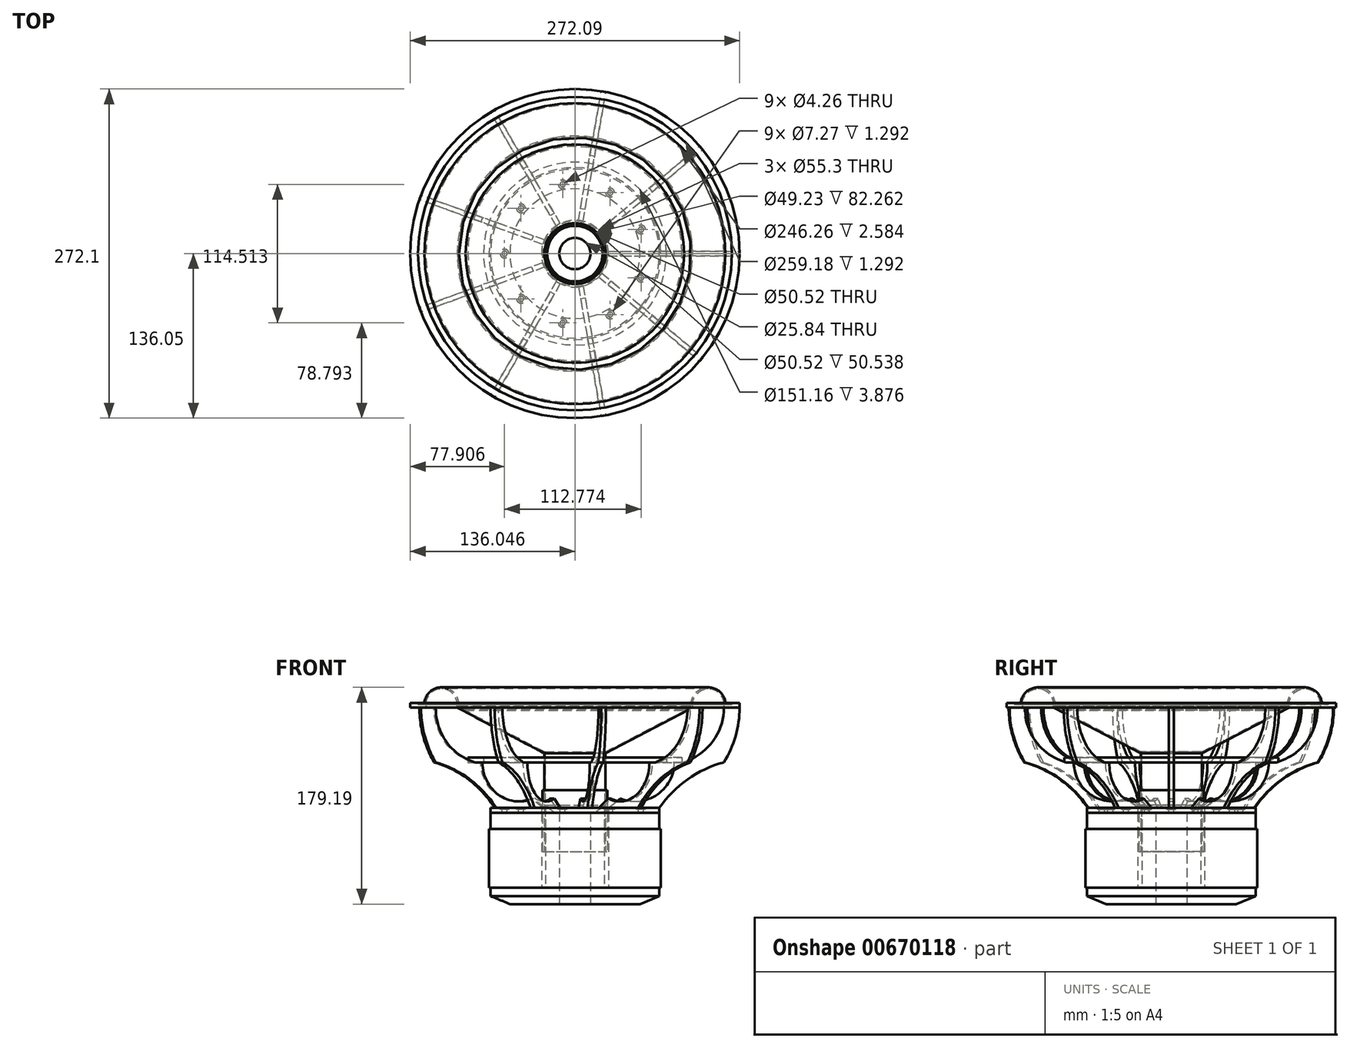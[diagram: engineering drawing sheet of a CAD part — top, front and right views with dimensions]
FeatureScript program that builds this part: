
annotation { "Feature Type Name" : "Feature", "Feature Type Description" : "" }
export const myFeature = defineFeature(function(context is Context, id is Id, definition is map)
    precondition{}
    {
        {
            var Q0;
            Q0=qCreatedBy(makeId("Front.planeOp"),FACE);
            var sketch = newSketch(context, id + "F0", { "sketchPlane" : qUnion([Q0])});
            skLineSegment(sketch, "E0.bottom", {"start": v(42.8, 0) * mm, "end": v(108, 0) * mm});
            skLineSegment(sketch, "E0.top", {"start": v(42.8, -6) * mm, "end": v(108, -6) * mm});
            skLineSegment(sketch, "E0.left", {"start": v(42.8, 0) * mm, "end": v(42.8, -6) * mm});
            skLineSegment(sketch, "E1", {"start": v(108, -6) * mm, "end": v(108, 0) * mm});
            skLineSegment(sketch, "E2", {"start": v(0, 0) * mm, "end": v(0, 32.36) * mm, "construction": true});
            skLineSegment(sketch, "E3.bottom", {"start": v(200.6, 134.34) * mm, "end": v(210.6, 134.34) * mm});
            skLineSegment(sketch, "E3.top", {"start": v(190.6, 128.34) * mm, "end": v(210.6, 128.34) * mm});
            skLineSegment(sketch, "E3.left", {"start": v(190.6, 132.34) * mm, "end": v(190.6, 128.34) * mm});
            skLineSegment(sketch, "E3.right", {"start": v(210.6, 134.34) * mm, "end": v(210.6, 128.34) * mm});
            skLineSegment(sketch, "E4", {"start": v(150.6, 128.34) * mm, "end": v(39.1, 70.03) * mm});
            skLineSegment(sketch, "E5", {"start": v(150.6, 130.03) * mm, "end": v(150.6, 128.34) * mm});
            skLineSegment(sketch, "E6", {"start": v(39.1, 71.72) * mm, "end": v(39.1, 70.03) * mm});
            skLineSegment(sketch, "E7.top", {"start": v(38.1, 71.72) * mm, "end": v(39.1, 71.72) * mm});
            skLineSegment(sketch, "E7.right", {"start": v(39.1, -55.62) * mm, "end": v(39.1, 71.72) * mm});
            skLineSegment(sketch, "E8", {"start": v(38.1, 71.72) * mm, "end": v(38.1, -55.62) * mm});
            skLineSegment(sketch, "E9", {"start": v(150.6, 130.03) * mm, "end": v(0, 130.03) * mm, "construction": true});
            skArc(sketch, "E10", {"start": v(0, 112.72) * mm, "mid": v(42.04, 108.02) * mm, "end": v(82, 94.16) * mm});
            skLineSegment(sketch, "E11", {"start": v(0, 112.72) * mm, "end": v(0, 111.72) * mm});
            skArc(sketch, "E12", {"start": v(0, 111.72) * mm, "mid": v(41.06, 106.82) * mm, "end": v(80.09, 93.16) * mm});
            skLineSegment(sketch, "E13", {"start": v(150.6, 130.03) * mm, "end": v(39.1, 71.72) * mm});
            skLineSegment(sketch, "E14", {"start": v(0, 112.72) * mm, "end": v(-8.95, 112.72) * mm, "construction": true});
            skLineSegment(sketch, "E15", {"start": v(190.6, 132.34) * mm, "end": v(200.6, 132.34) * mm});
            skLineSegment(sketch, "E16", {"start": v(200.6, 132.34) * mm, "end": v(200.6, 134.34) * mm});
            skLineSegment(sketch, "E17.right", {"start": v(110, -27) * mm, "end": v(110, -102) * mm});
            skLineSegment(sketch, "E18.top", {"start": v(108, -6) * mm, "end": v(42.8, -6) * mm});
            skLineSegment(sketch, "E18.left", {"start": v(108, -27) * mm, "end": v(108, -6) * mm});
            skLineSegment(sketch, "E18.right", {"start": v(42.8, -27) * mm, "end": v(42.8, -6) * mm});
            skLineSegment(sketch, "E19.top", {"start": v(83.05, -123) * mm, "end": v(20, -123) * mm});
            skLineSegment(sketch, "E19.left", {"start": v(108, -102) * mm, "end": v(108, -112.7) * mm});
            skLineSegment(sketch, "E19.right", {"start": v(20, -102) * mm, "end": v(20, -123) * mm});
            skLineSegment(sketch, "E20", {"start": v(108, -112.7) * mm, "end": v(83.05, -123) * mm});
            skPoint(sketch, "E21", {"position": v(42.8, -16.5) * mm});
            skLineSegment(sketch, "E22", {"start": v(139.64, 126.56) * mm, "end": v(140.57, 124.79) * mm});
            skArc(sketch, "E23", {"start": v(190.6, 132.34) * mm, "mid": v(169.38, 152.37) * mm, "end": v(150.6, 130.03) * mm});
            skLineSegment(sketch, "E24", {"start": v(200.6, 134.34) * mm, "end": v(192.5, 134.34) * mm});
            skLineSegment(sketch, "E25", {"start": v(139.64, 126.56) * mm, "end": v(148.5, 131.2) * mm});
            skArc(sketch, "E26", {"start": v(192.5, 134.34) * mm, "mid": v(168.96, 154.34) * mm, "end": v(148.5, 131.2) * mm});
            skLineSegment(sketch, "E27", {"start": v(192.5, 134.34) * mm, "end": v(190.5, 134.34) * mm, "construction": true});
            skLineSegment(sketch, "E28", {"start": v(127, 58.38) * mm, "end": v(127, 64.38) * mm});
            skLineSegment(sketch, "E29", {"start": v(117, 58.38) * mm, "end": v(42.8, 0) * mm, "construction": true});
            skLineSegment(sketch, "E30", {"start": v(150.6, 128.34) * mm, "end": v(150.6, 69.15) * mm, "construction": true});
            skCircle(sketch, "E31", {"center": v(170.53, 132.34) * mm, "radius": 20.07 * mm, "construction": true});
            skLineSegment(sketch, "E32", {"start": v(190.6, 128.34) * mm, "end": v(150.6, 69.15) * mm, "construction": true});
            skArc(sketch, "E33", {"start": v(190.46, 58.38) * mm, "mid": v(205.46, 91.94) * mm, "end": v(210.6, 128.34) * mm});
            skLineSegment(sketch, "E34.left", {"start": v(117, 58.38) * mm, "end": v(117, 64.38) * mm});
            skPoint(sketch, "E34.middle", {"position": v(127, 61.38) * mm});
            skLineSegment(sketch, "E35", {"start": v(137, 58.38) * mm, "end": v(137, 64.38) * mm});
            skLineSegment(sketch, "E36", {"start": v(137, 64.38) * mm, "end": v(117, 64.38) * mm});
            skArc(sketch, "E37", {"start": v(190.6, 128.34) * mm, "mid": v(175.66, 84.27) * mm, "end": v(137, 58.38) * mm});
            skPoint(sketch, "E38.endSnap0", {"position": v(75.4, 0) * mm});
            skLineSegment(sketch, "E39", {"start": v(42.8, 0) * mm, "end": v(58.05, 12) * mm});
            skLineSegment(sketch, "E40", {"start": v(58.05, 12) * mm, "end": v(58.05, 0) * mm});
            skArc(sketch, "E41", {"start": v(127, 58.38) * mm, "mid": v(104.88, 16.83) * mm, "end": v(58.05, 12) * mm});
            skLineSegment(sketch, "E42", {"start": v(127, 58.38) * mm, "end": v(137, 58.38) * mm});
            skLineSegment(sketch, "E43", {"start": v(127, 58.38) * mm, "end": v(117, 58.38) * mm});
            skLineSegment(sketch, "E44", {"start": v(117, 64.38) * mm, "end": v(117, 110.77) * mm, "construction": true});
            skLineSegment(sketch, "E45", {"start": v(196.55, 134.34) * mm, "end": v(196.55, 140.34) * mm});
            skLineSegment(sketch, "E46", {"start": v(196.55, 140.34) * mm, "end": v(226.55, 140.34) * mm});
            skLineSegment(sketch, "E47", {"start": v(226.55, 140.34) * mm, "end": v(226.55, 134.34) * mm});
            skLineSegment(sketch, "E48", {"start": v(226.55, 134.34) * mm, "end": v(210.6, 134.34) * mm});
            skLineSegment(sketch, "E49", {"start": v(38.1, -55.62) * mm, "end": v(41.66, -55.62) * mm});
            skLineSegment(sketch, "E50", {"start": v(41.66, -55.62) * mm, "end": v(41.66, 22.62) * mm});
            skLineSegment(sketch, "E51", {"start": v(41.66, 22.62) * mm, "end": v(39.1, 22.62) * mm});
            skLineSegment(sketch, "E52", {"start": v(42.8, -27) * mm, "end": v(42.8, -102) * mm});
            skPoint(sketch, "E53", {"position": v(41.66, -16.5) * mm});
            skLineSegment(sketch, "E54", {"start": v(42.8, -27) * mm, "end": v(110, -27) * mm});
            skLineSegment(sketch, "E55", {"start": v(20, -102) * mm, "end": v(110, -102) * mm});
            skLineSegment(sketch, "E56", {"start": v(110, -52.4) * mm, "end": v(42.8, -52.4) * mm});
            skLineSegment(sketch, "E57", {"start": v(110, -76.6) * mm, "end": v(42.8, -76.6) * mm});
            skArc(sketch, "E58", {"start": v(190.46, 58.38) * mm, "mid": v(143.97, 36.62) * mm, "end": v(108, 0) * mm});
            skLineSegment(sketch, "E59", {"start": v(39.1, -55.62) * mm, "end": v(39.1, -102) * mm, "construction": true});
            skLineSegment(sketch, "E60", {"start": v(58.05, 12) * mm, "end": v(58.05, 58.38) * mm, "construction": true});
            skLineSegment(sketch, "E61", {"start": v(20, -102) * mm, "end": v(20, -6) * mm});
            skLineSegment(sketch, "E62", {"start": v(37.5, -102) * mm, "end": v(37.5, 3.38) * mm});
            skArc(sketch, "E63", {"start": v(20, -6) * mm, "mid": v(29.06, -3.47) * mm, "end": v(35.5, 3.38) * mm});
            skLineSegment(sketch, "E64", {"start": v(20, -6) * mm, "end": v(0, -6) * mm, "construction": true});
            skLineSegment(sketch, "E65", {"start": v(35.5, 3.38) * mm, "end": v(37.5, 3.38) * mm});
            skSolve(sketch);
        }
        {
            var Q0;
            Q0=makeQuery(id+"F0.imprint","IMPRINT",FACE,{"disambiguationData":[TD([[makeQuery(id+"F0.imprint","IMPRINT",EDGE,{"derivedFrom":sQuery(id+"F0.wireOp",EDGE,"E0.bottom")}),1.0]])]});
            var Q1;
            Q1=makeQuery(id+"F0.imprint","IMPRINT",FACE,{"disambiguationData":[TD([[makeQuery(id+"F0.imprint","IMPRINT",EDGE,{"derivedFrom":sQuery(id+"F0.wireOp",EDGE,"E3.top")}),-1.0]])]});
            extrude(context, id + "F1", {"entities" : qUnion([Q0, Q1]), "depth" : 3 * mm, "hasSecondDirection" : true, "secondDirectionOppositeDirection" : true, "secondDirectionDepth" : 3 * mm});
        }
        {
            var Q0;
            Q0=makeQuery(id+"F1.opExtrude","SWEPT_BODY",BODY,{"disambiguationData":[OSD([sQuery(id+"F0.wireOp",EDGE,"E0.bottom"),sQuery(id+"F0.wireOp",EDGE,"6c7cb310-9df3-4df2-87a5-b65033ba0822.top"),sQuery(id+"F0.wireOp",EDGE,"nT3Qd54m-n4Mr-KzPj-ubfg-OKSk5NO6LqhC"),sQuery(id+"F0.wireOp",EDGE,"HfDnNz2e-wXp7-ltQI-1r98-O9Q1wdCByFx3"),sQuery(id+"F0.wireOp",EDGE,"b51f060f-5979-43c8-a97c-01c7b52eec3f")])]});
            var Q1;
            Q1=makeQuery(id+"F1.opExtrude","SWEPT_BODY",BODY,{"disambiguationData":[OSD([sQuery(id+"F0.wireOp",EDGE,"56108468-e6ef-4c31-aa1b-a381e27727b4.top"),sQuery(id+"F0.wireOp",EDGE,"E3.top"),sQuery(id+"F0.wireOp",EDGE,"4c3c0eb7-8127-4a6f-916d-201b3557d1e0"),sQuery(id+"F0.wireOp",EDGE,"e00a4080-055f-4dc8-8bab-c810e85ee1ca"),sQuery(id+"F0.wireOp",EDGE,"936a3c3a-1da7-4d78-9b4e-07095c25ca2c"),sQuery(id+"F0.wireOp",EDGE,"0a553143-d006-4ff2-9b8a-ab2828d84b0a")])]});
            var Q2;
            Q2=sQuery(id+"F0.wireOp",EDGE,"E2");
            circularPattern(context, id + "F2", {"entities" : qUnion([Q0, Q1]), "axis" : qUnion([Q2]), "angle" : 360 * degree, "instanceCount" : 9, "equalSpace" : true});
        }
        {
            var Q0;
            Q0=makeQuery(id+"F0.imprint","IMPRINT",FACE,{"disambiguationData":[TD([[makeQuery(id+"F0.imprint","IMPRINT",EDGE,{"derivedFrom":sQuery(id+"F0.wireOp",EDGE,"E0.bottom")}),-1.0]])]});
            var Q1;
            Q1=makeQuery(id+"F0.imprint","IMPRINT",FACE,{"disambiguationData":[TD([[makeQuery(id+"F0.imprint","IMPRINT",EDGE,{"derivedFrom":sQuery(id+"F0.wireOp",EDGE,"E4")}),-1.0]])]});
            var Q2;
            Q2=makeQuery(id+"F0.imprint","IMPRINT",FACE,{"disambiguationData":[TD([[makeQuery(id+"F0.imprint","IMPRINT",EDGE,{"derivedFrom":sQuery(id+"F0.wireOp",EDGE,"E3.bottom")}),-1.0]])]});
            var Q3;
            {var subQ0=sQuery(id+"F0.wireOp",EDGE,"E28");Q3=makeQuery(id+"F0.imprint","IMPRINT",FACE,{"disambiguationData":[TD([[makeQuery(id+"F0.imprint","IMPRINT",EDGE,{"derivedFrom":subQ0}),-1.0]])]});}
            var Q4;
            {var subQ0=sQuery(id+"F0.wireOp",EDGE,"E28");Q4=makeQuery(id+"F0.imprint","IMPRINT",FACE,{"disambiguationData":[TD([[makeQuery(id+"F0.imprint","IMPRINT",EDGE,{"derivedFrom":subQ0}),1.0]])]});}
            var Q5;
            {var subQ6=sQuery(id+"F0.wireOp",EDGE,"E56");Q5=makeQuery(id+"F0.imprint","IMPRINT",FACE,{"disambiguationData":[TD([[makeQuery(id+"F0.imprint","IMPRINT",EDGE,{"derivedFrom":subQ6}),-1.0]])]});}
            var Q6;
            {var subQ0=sQuery(id+"F0.wireOp",EDGE,"E56");Q6=makeQuery(id+"F0.imprint","IMPRINT",FACE,{"disambiguationData":[TD([[makeQuery(id+"F0.imprint","IMPRINT",EDGE,{"derivedFrom":subQ0}),1.0]])]});}
            var Q7;
            {var subQ6=sQuery(id+"F0.wireOp",EDGE,"E57");Q7=makeQuery(id+"F0.imprint","IMPRINT",FACE,{"disambiguationData":[TD([[makeQuery(id+"F0.imprint","IMPRINT",EDGE,{"derivedFrom":subQ6}),1.0]])]});}
            var Q8;
            {var subQ4=sQuery(id+"F0.wireOp",EDGE,"E50");Q8=makeQuery(id+"F0.imprint","IMPRINT",FACE,{"disambiguationData":[TD([[makeQuery(id+"F0.imprint","IMPRINT",EDGE,{"derivedFrom":subQ4}),1.0]])]});}
            var Q9;
            Q9=sQuery(id+"F0.wireOp",EDGE,"E2");
            revolve(context, id + "F3", {"entities" : qUnion([Q0, Q1, Q2, Q3, Q4, Q5, Q6, Q7, Q8]), "axis" : qUnion([Q9]), "revolveType" : RevolveType.FULL});
        }
        {
            var Q0;
            {var subQ5=sQuery(id+"F0.wireOp",EDGE,"E7.top");Q0=makeQuery(id+"F0.imprint","IMPRINT",FACE,{"disambiguationData":[TD([[makeQuery(id+"F0.imprint","IMPRINT",EDGE,{"derivedFrom":subQ5}),-1.0]])]});}
            var Q1;
            {var subQ0=sQuery(id+"F0.wireOp",EDGE,"E10");Q1=makeQuery(id+"F0.imprint","IMPRINT",FACE,{"disambiguationData":[TD([[makeQuery(id+"F0.imprint","IMPRINT",EDGE,{"derivedFrom":subQ0}),-1.0]])]});}
            var Q2;
            {var subQ3=sQuery(id+"F0.wireOp",EDGE,"E18.left");Q2=makeQuery(id+"F0.imprint","IMPRINT",FACE,{"disambiguationData":[TD([[makeQuery(id+"F0.imprint","IMPRINT",EDGE,{"derivedFrom":subQ3}),1.0]])]});}
            var Q3;
            Q3=makeQuery(id+"F0.imprint","IMPRINT",FACE,{"disambiguationData":[TD([[makeQuery(id+"F0.imprint","IMPRINT",EDGE,{"derivedFrom":sQuery(id+"F0.wireOp",EDGE,"E19.top")}),-1.0]])]});
            var Q4;
            Q4=makeQuery(id+"F0.imprint","IMPRINT",FACE,{"disambiguationData":[TD([[makeQuery(id+"F0.imprint","IMPRINT",EDGE,{"derivedFrom":sQuery(id+"F0.wireOp",EDGE,"E15")}),1.0]])]});
            var Q5;
            {var subQ1=sQuery(id+"F0.wireOp",EDGE,"E61");Q5=makeQuery(id+"F0.imprint","IMPRINT",FACE,{"disambiguationData":[TD([[makeQuery(id+"F0.imprint","IMPRINT",EDGE,{"derivedFrom":subQ1}),-1.0]])]});}
            var Q6;
            Q6=sQuery(id+"F0.wireOp",EDGE,"E2");
            revolve(context, id + "F4", {"entities" : qUnion([Q0, Q1, Q2, Q3, Q4, Q5]), "axis" : qUnion([Q6]), "revolveType" : RevolveType.FULL});
        }
        {
            var Q0;
            Q0=makeQuery(id+"F3.opRevolve","SWEPT_FACE",FACE,{"disambiguationData":[OSD([sQuery(id+"F0.wireOp",EDGE,"E0.bottom")])]});
            var sketch = newSketch(context, id + "F5", { "sketchPlane" : qUnion([Q0])});
            skPoint(sketch, "E66", {"position": v(-90, 0) * mm});
            skPoint(sketch, "E67.1.0", {"position": v(-68.94, -57.85) * mm});
            skPoint(sketch, "E67.2.0", {"position": v(-15.63, -88.63) * mm});
            skPoint(sketch, "E67.3.0", {"position": v(45, -77.94) * mm});
            skPoint(sketch, "E67.4.0", {"position": v(84.57, -30.78) * mm});
            skPoint(sketch, "E67.center", {"position": v(0, 0) * mm});
            skPoint(sketch, "E68.0.5.0", {"position": v(84.57, 30.78) * mm});
            skPoint(sketch, "E69.0.6.0", {"position": v(45, 77.94) * mm});
            skPoint(sketch, "E69.0.7.0", {"position": v(-15.63, 88.63) * mm});
            skPoint(sketch, "E69.0.8.0", {"position": v(-68.94, 57.85) * mm});
            skSolve(sketch);
        }
        {
            var Q0;
            Q0=sQuery(id+"F5.wireOp",VERTEX,"E66");
            var Q1;
            Q1=sQuery(id+"F5.wireOp",VERTEX,"E67.4.0");
            var Q2;
            Q2=sQuery(id+"F5.wireOp",VERTEX,"E67.3.0");
            var Q3;
            Q3=sQuery(id+"F5.wireOp",VERTEX,"E67.2.0");
            var Q4;
            Q4=sQuery(id+"F5.wireOp",VERTEX,"E67.1.0");
            var Q5;
            Q5=sQuery(id+"F5.wireOp",VERTEX,"E68.0.5.0");
            var Q6;
            Q6=sQuery(id+"F5.wireOp",VERTEX,"E69.0.7.0");
            var Q7;
            Q7=sQuery(id+"F5.wireOp",VERTEX,"E69.0.8.0");
            var Q8;
            Q8=sQuery(id+"F5.wireOp",VERTEX,"E69.0.6.0");
            var Q9;
            Q9=makeQuery(id+"F3.opRevolve","SWEPT_BODY",BODY,{"disambiguationData":[OSD([sQuery(id+"F0.wireOp",EDGE,"E0.bottom"),sQuery(id+"F0.wireOp",EDGE,"E0.left"),sQuery(id+"F0.wireOp",EDGE,"E1"),sQuery(id+"F0.wireOp",EDGE,"E18.top")])]});
            hole(context, id + "F6", {"style" : HoleStyle.C_BORE, "endStyle" : HoleEndStyle.THROUGH, "holeDiameter" : 6.6 * mm, "cBoreDiameter" : 11.25 * mm, "cBoreDepth" : 2 * mm, "locations" : qUnion([Q0, Q1, Q2, Q3, Q4, Q5, Q6, Q7, Q8]), "scope" : qUnion([Q9]), "tappedDepth" : 12 * mm, "tapClearance" : 3});
        }
        {
            var Q0;
            Q0=makeQuery(id+"F3.opRevolve","SWEPT_BODY",BODY,{"disambiguationData":[OSD([sQuery(id+"F0.wireOp",EDGE,"E3.bottom"),sQuery(id+"F0.wireOp",EDGE,"E3.top"),sQuery(id+"F0.wireOp",EDGE,"E3.left"),sQuery(id+"F0.wireOp",EDGE,"E3.right"),sQuery(id+"F0.wireOp",EDGE,"E15"),sQuery(id+"F0.wireOp",EDGE,"E16")])]});
            var Q1;
            Q1=makeQuery(id+"F1.opExtrude","SWEPT_BODY",BODY,{"disambiguationData":[OSD([sQuery(id+"F0.wireOp",EDGE,"E0.bottom"),sQuery(id+"F0.wireOp",EDGE,"E3.top"),sQuery(id+"F0.wireOp",EDGE,"E33"),sQuery(id+"F0.wireOp",EDGE,"E37"),sQuery(id+"F0.wireOp",EDGE,"E39"),sQuery(id+"F0.wireOp",EDGE,"E41"),sQuery(id+"F0.wireOp",EDGE,"E42"),sQuery(id+"F0.wireOp",EDGE,"E58")])]});
            var Q2;
            Q2=makeQuery(id+"F2.opPattern","COPY",BODY,{"derivedFrom":makeQuery(id+"F1.opExtrude","SWEPT_BODY",BODY,{"disambiguationData":[OSD([sQuery(id+"F0.wireOp",EDGE,"E0.bottom"),sQuery(id+"F0.wireOp",EDGE,"E3.top"),sQuery(id+"F0.wireOp",EDGE,"E33"),sQuery(id+"F0.wireOp",EDGE,"E37"),sQuery(id+"F0.wireOp",EDGE,"E39"),sQuery(id+"F0.wireOp",EDGE,"E41"),sQuery(id+"F0.wireOp",EDGE,"E42"),sQuery(id+"F0.wireOp",EDGE,"E58")])]}),"instanceName":"1"});
            var Q3;
            Q3=makeQuery(id+"F2.opPattern","COPY",BODY,{"derivedFrom":makeQuery(id+"F1.opExtrude","SWEPT_BODY",BODY,{"disambiguationData":[OSD([sQuery(id+"F0.wireOp",EDGE,"E0.bottom"),sQuery(id+"F0.wireOp",EDGE,"E3.top"),sQuery(id+"F0.wireOp",EDGE,"E33"),sQuery(id+"F0.wireOp",EDGE,"E37"),sQuery(id+"F0.wireOp",EDGE,"E39"),sQuery(id+"F0.wireOp",EDGE,"E41"),sQuery(id+"F0.wireOp",EDGE,"E42"),sQuery(id+"F0.wireOp",EDGE,"E58")])]}),"instanceName":"2"});
            var Q4;
            Q4=makeQuery(id+"F2.opPattern","COPY",BODY,{"derivedFrom":makeQuery(id+"F1.opExtrude","SWEPT_BODY",BODY,{"disambiguationData":[OSD([sQuery(id+"F0.wireOp",EDGE,"E0.bottom"),sQuery(id+"F0.wireOp",EDGE,"E3.top"),sQuery(id+"F0.wireOp",EDGE,"E33"),sQuery(id+"F0.wireOp",EDGE,"E37"),sQuery(id+"F0.wireOp",EDGE,"E39"),sQuery(id+"F0.wireOp",EDGE,"E41"),sQuery(id+"F0.wireOp",EDGE,"E42"),sQuery(id+"F0.wireOp",EDGE,"E58")])]}),"instanceName":"3"});
            var Q5;
            Q5=makeQuery(id+"F2.opPattern","COPY",BODY,{"derivedFrom":makeQuery(id+"F1.opExtrude","SWEPT_BODY",BODY,{"disambiguationData":[OSD([sQuery(id+"F0.wireOp",EDGE,"E0.bottom"),sQuery(id+"F0.wireOp",EDGE,"E3.top"),sQuery(id+"F0.wireOp",EDGE,"E33"),sQuery(id+"F0.wireOp",EDGE,"E37"),sQuery(id+"F0.wireOp",EDGE,"E39"),sQuery(id+"F0.wireOp",EDGE,"E41"),sQuery(id+"F0.wireOp",EDGE,"E42"),sQuery(id+"F0.wireOp",EDGE,"E58")])]}),"instanceName":"4"});
            var Q6;
            Q6=makeQuery(id+"F2.opPattern","COPY",BODY,{"derivedFrom":makeQuery(id+"F1.opExtrude","SWEPT_BODY",BODY,{"disambiguationData":[OSD([sQuery(id+"F0.wireOp",EDGE,"E0.bottom"),sQuery(id+"F0.wireOp",EDGE,"E3.top"),sQuery(id+"F0.wireOp",EDGE,"E33"),sQuery(id+"F0.wireOp",EDGE,"E37"),sQuery(id+"F0.wireOp",EDGE,"E39"),sQuery(id+"F0.wireOp",EDGE,"E41"),sQuery(id+"F0.wireOp",EDGE,"E42"),sQuery(id+"F0.wireOp",EDGE,"E58")])]}),"instanceName":"5"});
            var Q7;
            Q7=makeQuery(id+"F2.opPattern","COPY",BODY,{"derivedFrom":makeQuery(id+"F1.opExtrude","SWEPT_BODY",BODY,{"disambiguationData":[OSD([sQuery(id+"F0.wireOp",EDGE,"E0.bottom"),sQuery(id+"F0.wireOp",EDGE,"E3.top"),sQuery(id+"F0.wireOp",EDGE,"E33"),sQuery(id+"F0.wireOp",EDGE,"E37"),sQuery(id+"F0.wireOp",EDGE,"E39"),sQuery(id+"F0.wireOp",EDGE,"E41"),sQuery(id+"F0.wireOp",EDGE,"E42"),sQuery(id+"F0.wireOp",EDGE,"E58")])]}),"instanceName":"6"});
            var Q8;
            Q8=makeQuery(id+"F2.opPattern","COPY",BODY,{"derivedFrom":makeQuery(id+"F1.opExtrude","SWEPT_BODY",BODY,{"disambiguationData":[OSD([sQuery(id+"F0.wireOp",EDGE,"E0.bottom"),sQuery(id+"F0.wireOp",EDGE,"E3.top"),sQuery(id+"F0.wireOp",EDGE,"E33"),sQuery(id+"F0.wireOp",EDGE,"E37"),sQuery(id+"F0.wireOp",EDGE,"E39"),sQuery(id+"F0.wireOp",EDGE,"E41"),sQuery(id+"F0.wireOp",EDGE,"E42"),sQuery(id+"F0.wireOp",EDGE,"E58")])]}),"instanceName":"7"});
            var Q9;
            Q9=makeQuery(id+"F2.opPattern","COPY",BODY,{"derivedFrom":makeQuery(id+"F1.opExtrude","SWEPT_BODY",BODY,{"disambiguationData":[OSD([sQuery(id+"F0.wireOp",EDGE,"E0.bottom"),sQuery(id+"F0.wireOp",EDGE,"E3.top"),sQuery(id+"F0.wireOp",EDGE,"E33"),sQuery(id+"F0.wireOp",EDGE,"E37"),sQuery(id+"F0.wireOp",EDGE,"E39"),sQuery(id+"F0.wireOp",EDGE,"E41"),sQuery(id+"F0.wireOp",EDGE,"E42"),sQuery(id+"F0.wireOp",EDGE,"E58")])]}),"instanceName":"8"});
            var Q10;
            Q10=makeQuery(id+"F3.opRevolve","SWEPT_BODY",BODY,{"disambiguationData":[OSD([sQuery(id+"F0.wireOp",EDGE,"E0.bottom"),sQuery(id+"F0.wireOp",EDGE,"E0.left"),sQuery(id+"F0.wireOp",EDGE,"E1"),sQuery(id+"F0.wireOp",EDGE,"E18.top")])]});
            var Q11;
            Q11=makeQuery(id+"F3.opRevolve","SWEPT_BODY",BODY,{"disambiguationData":[OSD([sQuery(id+"F0.wireOp",EDGE,"E4"),sQuery(id+"F0.wireOp",EDGE,"E5"),sQuery(id+"F0.wireOp",EDGE,"E7.right"),sQuery(id+"F0.wireOp",EDGE,"E13")])]});
            var Q12;
            Q12=makeQuery(id+"F3.opRevolve","SWEPT_BODY",BODY,{"disambiguationData":[OSD([sQuery(id+"F0.wireOp",EDGE,"E7.right"),sQuery(id+"F0.wireOp",EDGE,"E49"),sQuery(id+"F0.wireOp",EDGE,"E50"),sQuery(id+"F0.wireOp",EDGE,"E51")])]});
            var Q13;
            Q13=makeQuery(id+"F3.opRevolve","SWEPT_BODY",BODY,{"disambiguationData":[OSD([sQuery(id+"F0.wireOp",EDGE,"E17.right"),sQuery(id+"F0.wireOp",EDGE,"E52"),sQuery(id+"F0.wireOp",EDGE,"E54"),sQuery(id+"F0.wireOp",EDGE,"E55")])]});
            var Q14;
            Q14=makeQuery(id+"F3.opRevolve","SWEPT_BODY",BODY,{"disambiguationData":[OSD([sQuery(id+"F0.wireOp",EDGE,"E34.left"),sQuery(id+"F0.wireOp",EDGE,"E35"),sQuery(id+"F0.wireOp",EDGE,"E36"),sQuery(id+"F0.wireOp",EDGE,"E42"),sQuery(id+"F0.wireOp",EDGE,"E43")])]});
            var Q15;
            Q15=makeQuery(id+"F4.opRevolve","SWEPT_BODY",BODY,{"disambiguationData":[OSD([sQuery(id+"F0.wireOp",EDGE,"E7.top"),sQuery(id+"F0.wireOp",EDGE,"E7.right"),sQuery(id+"F0.wireOp",EDGE,"E8"),sQuery(id+"F0.wireOp",EDGE,"E49")])]});
            var Q16;
            Q16=makeQuery(id+"F4.opRevolve","SWEPT_BODY",BODY,{"disambiguationData":[OSD([sQuery(id+"F0.wireOp",EDGE,"E10"),sQuery(id+"F0.wireOp",EDGE,"E11"),sQuery(id+"F0.wireOp",EDGE,"E12"),sQuery(id+"F0.wireOp",EDGE,"E13")])]});
            var Q17;
            Q17=makeQuery(id+"F4.opRevolve","SWEPT_BODY",BODY,{"disambiguationData":[OSD([sQuery(id+"F0.wireOp",EDGE,"E13"),sQuery(id+"F0.wireOp",EDGE,"E15"),sQuery(id+"F0.wireOp",EDGE,"E16"),sQuery(id+"F0.wireOp",EDGE,"E22"),sQuery(id+"F0.wireOp",EDGE,"E23"),sQuery(id+"F0.wireOp",EDGE,"E24"),sQuery(id+"F0.wireOp",EDGE,"E25"),sQuery(id+"F0.wireOp",EDGE,"E26")])]});
            var Q18;
            Q18=makeQuery(id+"F4.opRevolve","SWEPT_BODY",BODY,{"disambiguationData":[OSD([sQuery(id+"F0.wireOp",EDGE,"E18.top"),sQuery(id+"F0.wireOp",EDGE,"E18.left"),sQuery(id+"F0.wireOp",EDGE,"E18.right"),sQuery(id+"F0.wireOp",EDGE,"E54")])]});
            var Q19;
            Q19=makeQuery(id+"F4.opRevolve","SWEPT_BODY",BODY,{"disambiguationData":[OSD([sQuery(id+"F0.wireOp",EDGE,"E19.top"),sQuery(id+"F0.wireOp",EDGE,"E19.left"),sQuery(id+"F0.wireOp",EDGE,"E19.right"),sQuery(id+"F0.wireOp",EDGE,"E20"),sQuery(id+"F0.wireOp",EDGE,"E55"),sQuery(id+"F0.wireOp",EDGE,"E61"),sQuery(id+"F0.wireOp",EDGE,"E62"),sQuery(id+"F0.wireOp",EDGE,"E63"),sQuery(id+"F0.wireOp",EDGE,"E65")])]});
            var Q20;
            Q20=sQuery(id+"F0.wireOp",VERTEX,"E12.center");
            transform(context, id + "F7", {"entities" : qUnion([Q0, Q1, Q2, Q3, Q4, Q5, Q6, Q7, Q8, Q9, Q10, Q11, Q12, Q13, Q14, Q15, Q16, Q17, Q18, Q19]), "transformType" : TransformType.SCALE_UNIFORMLY, "scale" : .646, "scalePoint" : qUnion([Q20]), "makeCopy" : false});
        }
    });
